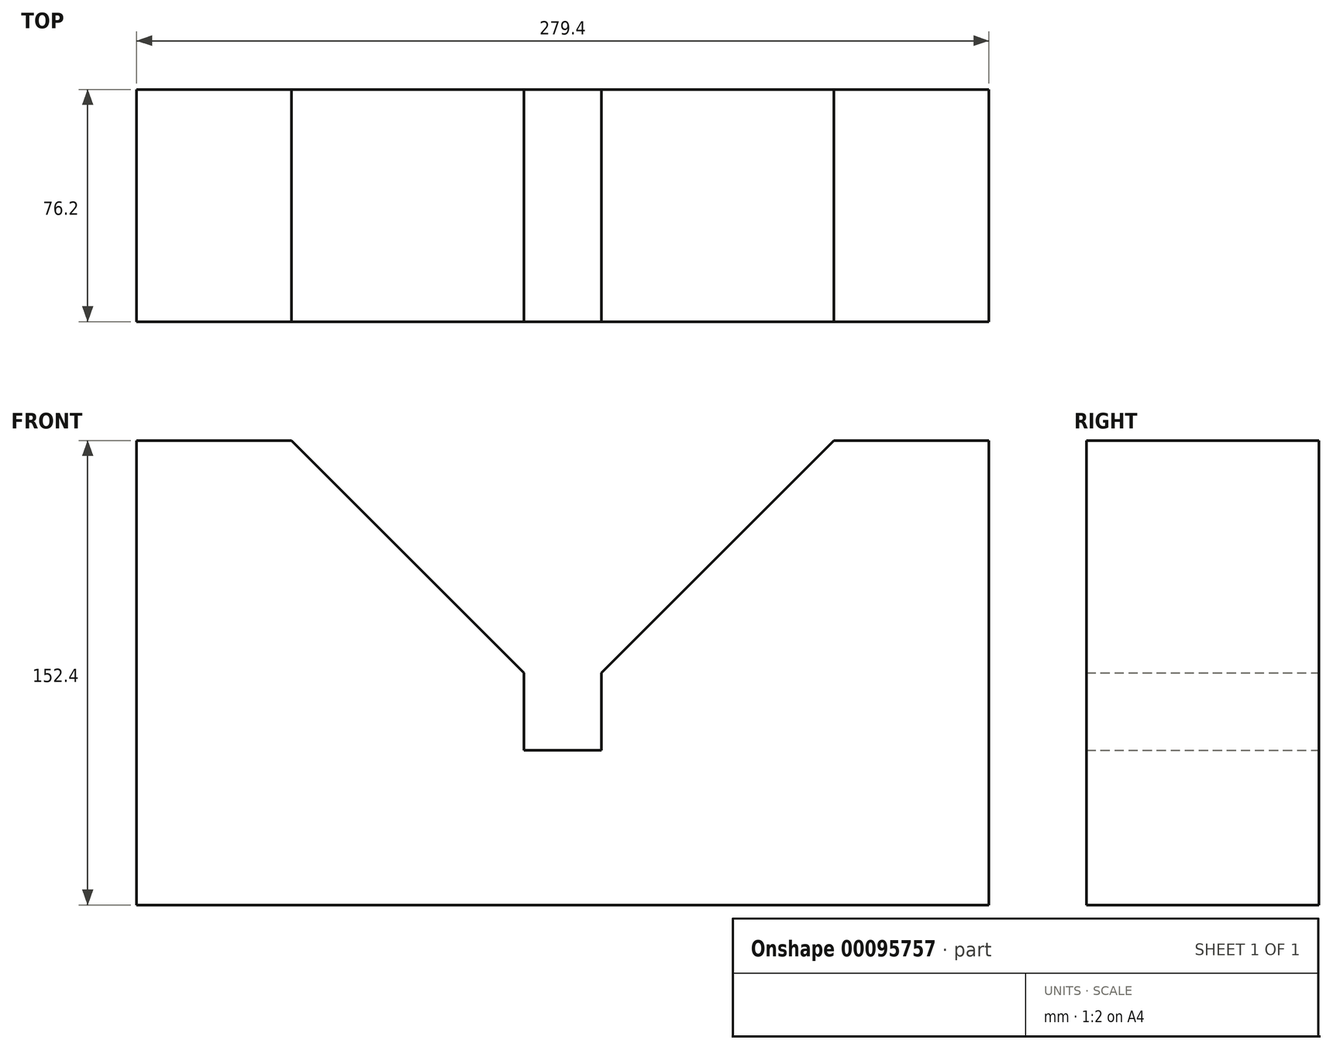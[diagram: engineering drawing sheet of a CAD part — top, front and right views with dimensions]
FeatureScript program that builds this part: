
annotation { "Feature Type Name" : "Feature", "Feature Type Description" : "" }
export const myFeature = defineFeature(function(context is Context, id is Id, definition is map)
    precondition{}
    {
        {
            var Q0;
            Q0=qCreatedBy(makeId("Front.planeOp"),FACE);
            var sketch = newSketch(context, id + "F0", { "sketchPlane" : qUnion([Q0])});
            skLineSegment(sketch, "E0.bottom", {"start": v(-96.1, 130.03) * mm, "end": v(-45.3, 130.03) * mm});
            skLineSegment(sketch, "E0.top", {"start": v(-96.1, -22.37) * mm, "end": v(-45.3, -22.37) * mm});
            skLineSegment(sketch, "E0.left", {"start": v(-96.1, 130.03) * mm, "end": v(-96.1, -22.37) * mm});
            skLineSegment(sketch, "E1.bottom", {"start": v(-45.3, -22.37) * mm, "end": v(30.9, -22.37) * mm});
            skLineSegment(sketch, "E1.top", {"start": v(-45.3, -22.37) * mm, "end": v(30.9, -22.37) * mm});
            skLineSegment(sketch, "E1.left", {"start": v(-45.3, -22.37) * mm, "end": v(-45.3, -22.37) * mm});
            skLineSegment(sketch, "E1.right", {"start": v(30.9, -22.37) * mm, "end": v(30.9, -22.37) * mm});
            skLineSegment(sketch, "E2.top", {"start": v(30.9, 53.83) * mm, "end": v(30.9, 53.83) * mm});
            skLineSegment(sketch, "E3", {"start": v(-45.3, 130.03) * mm, "end": v(30.9, 53.83) * mm});
            skLineSegment(sketch, "E4.MirrorCS", {"start": v(132.5, 130.03) * mm, "end": v(56.3, 53.83) * mm});
            skLineSegment(sketch, "E5.MirrorCS", {"start": v(132.5, -22.37) * mm, "end": v(56.3, -22.37) * mm});
            skLineSegment(sketch, "E6.MirrorCS", {"start": v(183.3, -22.37) * mm, "end": v(132.5, -22.37) * mm});
            skLineSegment(sketch, "E7.MirrorCS", {"start": v(183.3, 130.03) * mm, "end": v(183.3, -22.37) * mm});
            skLineSegment(sketch, "E8.MirrorCS", {"start": v(183.3, 130.03) * mm, "end": v(132.5, 130.03) * mm});
            skLineSegment(sketch, "E9", {"start": v(30.9, -22.37) * mm, "end": v(56.3, -22.37) * mm});
            skLineSegment(sketch, "E10.top", {"start": v(30.9, 28.43) * mm, "end": v(56.3, 28.43) * mm});
            skLineSegment(sketch, "E11", {"start": v(30.9, 53.83) * mm, "end": v(30.9, 28.43) * mm});
            skLineSegment(sketch, "E12", {"start": v(56.3, 53.83) * mm, "end": v(56.3, 28.43) * mm});
            skSolve(sketch);
        }
        {
            var Q0;
            Q0 = qSketchRegion(id + "F0", true);
            extrude(context, id + "F1", {"entities" : qUnion([Q0]), "depth" : 76.2 * mm});
        }
    });
